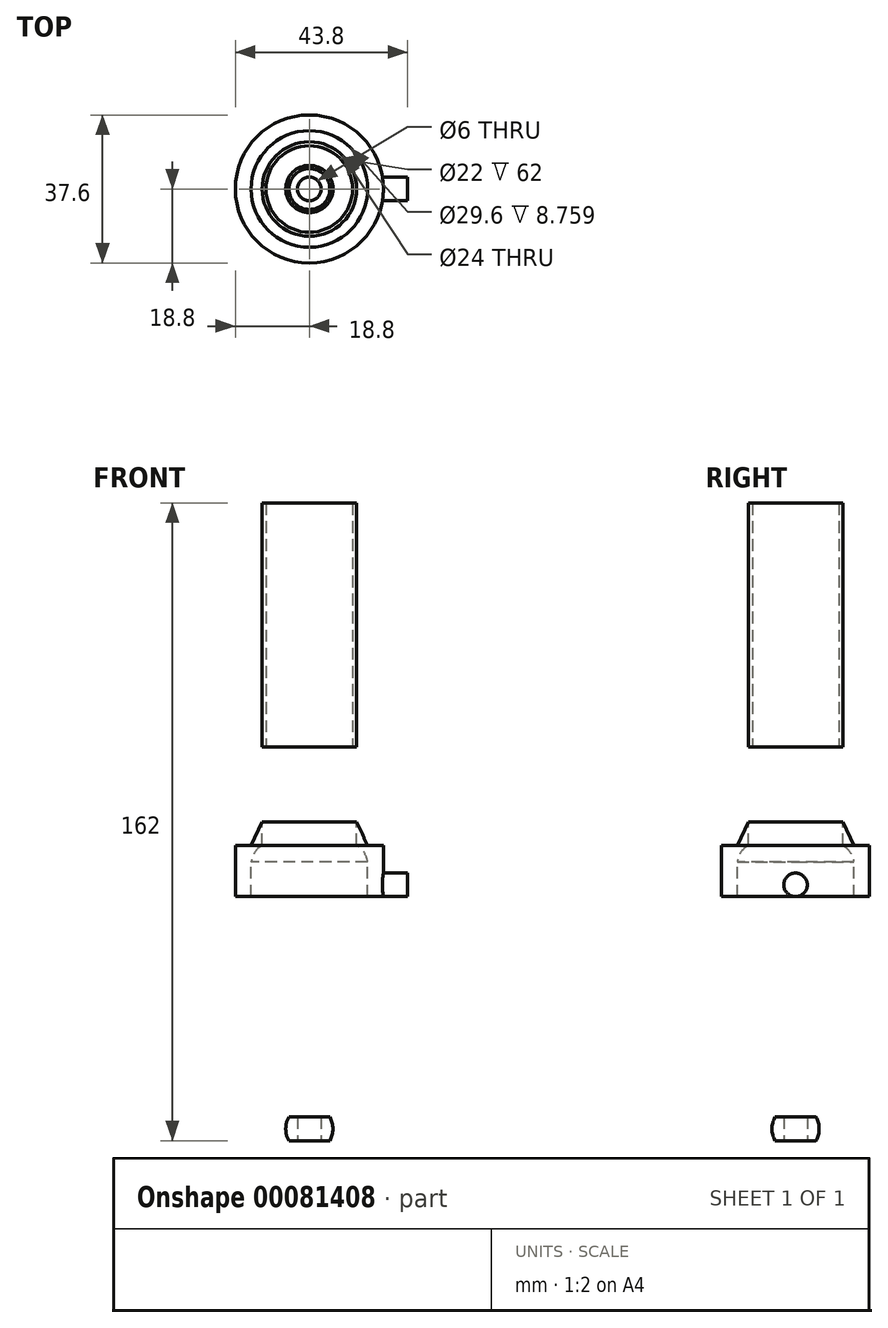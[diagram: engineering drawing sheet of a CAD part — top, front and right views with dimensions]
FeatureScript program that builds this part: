
annotation { "Feature Type Name" : "Feature", "Feature Type Description" : "" }
export const myFeature = defineFeature(function(context is Context, id is Id, definition is map)
    precondition{}
    {
        {
            var Q0;
            Q0=qCreatedBy(makeId("Top.planeOp"),FACE);
            var sketch = newSketch(context, id + "F0", { "sketchPlane" : qUnion([Q0])});
            skCircle(sketch, "E0", {"center": v(0, 0) * mm, "radius": 11 * mm});
            skCircle(sketch, "E1", {"center": v(0, 0) * mm, "radius": 12 * mm});
            skSolve(sketch);
        }
        {
            var Q0;
            Q0 = qSketchRegion(id + "F0", true);
            extrude(context, id + "F1", {"entities" : qUnion([Q0]), "depth" : 6 * mm});
        }
        {
            var Q0;
            Q0=makeQuery(id+"F1.opExtrude","CAP_FACE",FACE,{"disambiguationData":[OSD([sQuery(id+"F0.wireOp",EDGE,"E0"),sQuery(id+"F0.wireOp",EDGE,"E1")])],"isStart":false});
            var sketch = newSketch(context, id + "F2", { "sketchPlane" : qUnion([Q0])});
            skSolve(sketch);
        }
        {
            var Q0;
            Q0=makeQuery(id+"F2.imprint","IMPRINT",FACE,{"disambiguationData":[TD([[makeQuery(id+"F2.imprint","IMPRINT",EDGE,{"derivedFrom":makeQuery(id+"F1.opExtrude","CAP_EDGE",EDGE,{"disambiguationData":[OSD([sQuery(id+"F0.wireOp",EDGE,"E0")])],"isStart":false})}),-1.0]])]});
            extrude(context, id + "F3", {"entities" : qUnion([Q0]), "operationType" : NewBodyOperationType.ADD, "depth" : (62 - 6) * mm});
        }
        {
            var Q0;
            Q0=makeQuery(id+"F1.opExtrude","SWEPT_BODY",BODY,{"disambiguationData":[OSD([sQuery(id+"F0.wireOp",EDGE,"E0"),sQuery(id+"F0.wireOp",EDGE,"E1")])]});
            transform(context, id + "F4", {"entities" : qUnion([Q0]), "transformType" : TransformType.TRANSLATION_3D, "dx" : 0 * mm, "dy" : 0 * mm, "dz" : 100 * mm, "makeCopy" : false});
        }
        {
            var Q0;
            Q0=qCreatedBy(makeId("Front.planeOp"),FACE);
            var sketch = newSketch(context, id + "F5", { "sketchPlane" : qUnion([Q0])});
            skLineSegment(sketch, "E2", {"start": v(0, 0) * mm, "end": v(12, 0) * mm});
            skLineSegment(sketch, "E3", {"start": v(12, 0) * mm, "end": v(12, 6) * mm});
            skLineSegment(sketch, "E4", {"start": v(12, 6) * mm, "end": v(14.8, 0) * mm});
            skLineSegment(sketch, "E5", {"start": v(12, 0) * mm, "end": v(14.8, 0) * mm});
            skLineSegment(sketch, "E6", {"start": v(0, 4.05) * mm, "end": v(0, 0) * mm});
            skLineSegment(sketch, "E7", {"start": v(14.8, 0) * mm, "end": v(18.8, 0) * mm});
            skLineSegment(sketch, "E8", {"start": v(18.8, 0) * mm, "end": v(18.8, -13) * mm});
            skLineSegment(sketch, "E9", {"start": v(18.8, -13) * mm, "end": v(14.8, -13) * mm});
            skLineSegment(sketch, "E10", {"start": v(14.8, -13) * mm, "end": v(14.8, 0) * mm});
            skArc(sketch, "E11", {"start": v(14.8, -5.44) * mm, "mid": v(14.22, -2.3) * mm, "end": v(12, 0) * mm});
            skSolve(sketch);
        }
        {
            var Q0;
            Q0 = qSketchRegion(id + "F5", true);
            var Q1;
            Q1=sQuery(id+"F5.wireOp",EDGE,"E6");
            revolve(context, id + "F6", {"entities" : qUnion([Q0]), "axis" : qUnion([Q1]), "revolveType" : RevolveType.FULL});
        }
        {
            var Q0;
            Q0=qCreatedBy(makeId("Right.planeOp"),FACE);
            var sketch = newSketch(context, id + "F7", { "sketchPlane" : qUnion([Q0])});
            skLineSegment(sketch, "E12", {"start": v(0, 0) * mm, "end": v(0, -10) * mm});
            skCircle(sketch, "E13", {"center": v(0, -10) * mm, "radius": 3 * mm});
            skSolve(sketch);
        }
        {
            var Q0;
            Q0=makeQuery(id+"F7.imprint","IMPRINT",FACE,{"disambiguationData":[TD([[makeQuery(id+"F7.imprint","IMPRINT",EDGE,{"derivedFrom":sQuery(id+"F7.wireOp",EDGE,"E13")}),1.0]])]});
            extrude(context, id + "F8", {"entities" : qUnion([Q0]), "operationType" : NewBodyOperationType.ADD, "depth" : 25 * mm});
        }
        {
            var Q0;
            Q0=makeQuery(id+"F6.opRevolve","SWEPT_FACE",FACE,{"disambiguationData":[OSD([sQuery(id+"F5.wireOp",EDGE,"E9")])]});
            var sketch = newSketch(context, id + "F9", { "sketchPlane" : qUnion([Q0])});
            skSolve(sketch);
        }
        {
            var Q0;
            Q0=makeQuery(id+"F9.imprint","IMPRINT",FACE,{"disambiguationData":[TD([[makeQuery(id+"F9.imprint","IMPRINT",EDGE,{"derivedFrom":makeQuery(id+"F6.opRevolve","SWEPT_EDGE",EDGE,{"disambiguationData":[OSD([sQuery(id+"F5.wireOp",EDGE,"E9"),sQuery(id+"F5.wireOp",EDGE,"E10")])]})}),-1.0]])]});
            extrude(context, id + "F10", {"entities" : qUnion([Q0]), "operationType" : NewBodyOperationType.REMOVE, "oppositeDirection" : true, "depth" : 6.1 * mm});
        }
        {
            var Q0;
            Q0=makeQuery(id+"F6.opRevolve","SWEPT_BODY",BODY,{"disambiguationData":[OSD([sQuery(id+"F5.wireOp",EDGE,"E3"),sQuery(id+"F5.wireOp",EDGE,"E4"),sQuery(id+"F5.wireOp",EDGE,"E7"),sQuery(id+"F5.wireOp",EDGE,"E8"),sQuery(id+"F5.wireOp",EDGE,"E9"),sQuery(id+"F5.wireOp",EDGE,"E10"),sQuery(id+"F5.wireOp",EDGE,"E11")])]});
            transform(context, id + "F11", {"entities" : qUnion([Q0]), "transformType" : TransformType.TRANSLATION_3D, "dx" : 0 * mm, "dy" : 0 * mm, "dz" : 75 * mm, "makeCopy" : false});
        }
        {
            var Q0;
            Q0=qCreatedBy(makeId("Right.planeOp"),FACE);
            var sketch = newSketch(context, id + "F12", { "sketchPlane" : qUnion([Q0])});
            skLineSegment(sketch, "E14", {"start": v(0, 0) * mm, "end": v(0, 6) * mm});
            skArc(sketch, "E15", {"start": v(5.2, 0) * mm, "mid": v(6, 3) * mm, "end": v(5.2, 6) * mm});
            skLineSegment(sketch, "E16", {"start": v(3, 6) * mm, "end": v(5.2, 6) * mm});
            skLineSegment(sketch, "E17", {"start": v(0, 0) * mm, "end": v(5.2, 0) * mm});
            skLineSegment(sketch, "E18", {"start": v(0, 0) * mm, "end": v(3, 0) * mm});
            skLineSegment(sketch, "E19", {"start": v(3, 0) * mm, "end": v(3, 6) * mm});
            skSolve(sketch);
        }
        {
            var Q0;
            Q0 = qSketchRegion(id + "F12", true);
            var Q1;
            Q1=sQuery(id+"F12.wireOp",EDGE,"E14");
            revolve(context, id + "F13", {"entities" : qUnion([Q0]), "axis" : qUnion([Q1]), "revolveType" : RevolveType.FULL});
        }
    });
